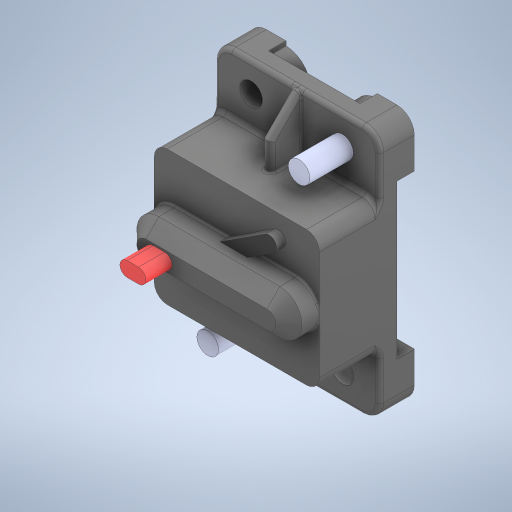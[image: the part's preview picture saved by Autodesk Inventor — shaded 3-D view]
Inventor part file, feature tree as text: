
AUTODESK INVENTOR PART (.ipt)
format: ipt  version: 2024.2 (Build 282272000, 272)  size: 513,024 bytes
history: native  units: in
note: dims shown in document units (in); Inventor stores cm internally (conversion verified against a paired STEP export)
features: sketch x1, other x1
ambient origin geometry x8: Origin, YZ Plane, XZ Plane, XY Plane, X Axis, Y Axis, Z Axis, Center Point
bodies: Solid1 (feature_tree)
feature tree (2):
  sketch  "Sketch1"  dims[d0=2.23in d1=1.05in]
  other  "Breaker, Main, 120A"
